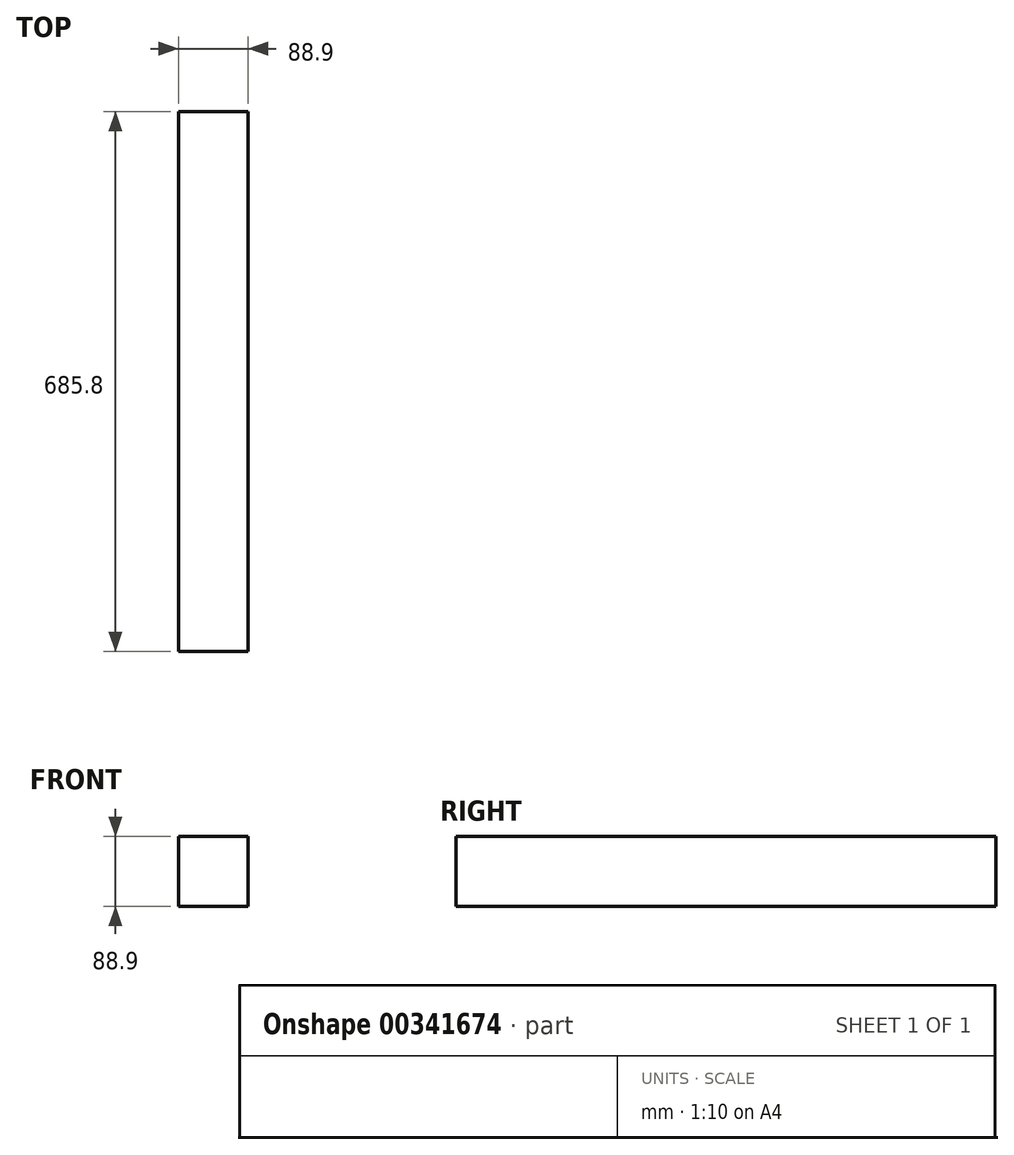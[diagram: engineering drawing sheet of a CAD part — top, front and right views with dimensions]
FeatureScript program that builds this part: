
annotation { "Feature Type Name" : "Feature", "Feature Type Description" : "" }
export const myFeature = defineFeature(function(context is Context, id is Id, definition is map)
    precondition{}
    {
        {
            var Q0;
            Q0=qCreatedBy(makeId("Right.planeOp"),FACE);
            var sketch = newSketch(context, id + "F0", { "sketchPlane" : qUnion([Q0])});
            skLineSegment(sketch, "E0.bottom", {"start": v(-333.55, 85.76) * mm, "end": v(352.25, 85.76) * mm});
            skLineSegment(sketch, "E0.top", {"start": v(-333.55, -3.14) * mm, "end": v(352.25, -3.14) * mm});
            skLineSegment(sketch, "E0.left", {"start": v(-333.55, 85.76) * mm, "end": v(-333.55, -3.14) * mm});
            skLineSegment(sketch, "E0.right", {"start": v(352.25, 85.76) * mm, "end": v(352.25, -3.14) * mm});
            skSolve(sketch);
        }
        {
            var Q0;
            Q0=makeQuery(id+"F0.imprint","IMPRINT",FACE,{"disambiguationData":[TD([[makeQuery(id+"F0.imprint","IMPRINT",EDGE,{"derivedFrom":sQuery(id+"F0.wireOp",EDGE,"E0.bottom")}),-1.0]])]});
            extrude(context, id + "F1", {"entities" : qUnion([Q0]), "depth" : 88.9 * mm});
        }
    });
